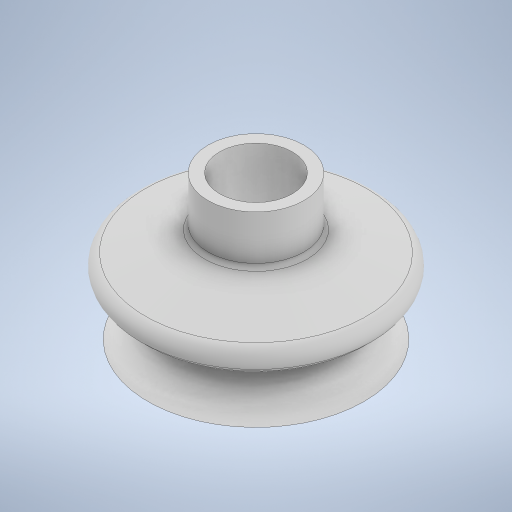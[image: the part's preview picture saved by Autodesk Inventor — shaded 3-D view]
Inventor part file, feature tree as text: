
AUTODESK INVENTOR PART (.ipt)
format: ipt  version: 2024 (Build 280153000, 153)  size: 373,248 bytes
history: native  units: mm
features: other x3, extrude x3, fillet x3, chamfer x2, revolve x1, hole x1, sketch x1
ambient origin geometry x8: Origin, YZ Plane, XZ Plane, XY Plane, X Axis, Y Axis, Z Axis, Center Point
bodies: Body1 (feature_tree)
feature tree (14):
  other  "Sólido1"
  extrude  "Extrusión1"  Depth=10.0mm TaperAngle=0.0deg
  extrude  "Extrusión2"  Depth=10.0mm
  extrude  "Extrusión3"  Depth=10.0mm TaperAngle=0.0deg
  chamfer  "Chaflán1"  Distance=20.0mm
  chamfer  "Chaflán2"  Distance=10.0mm
  fillet  "Empalme1"  Radius=15.0mm
  revolve  "Revolución1"  Angle=45.0deg
  fillet  "Empalme2"  Radius=2.5mm
  hole  "Agujero1"  [1 undecoded]
  fillet  "Empalme3"  [1 undecoded]
  other  "Edición directa1"
  sketch  "Boceto5"  dims[d0=45.0mm d1=10.0mm d2=0.0mm d3=50.0mm d4=10.0mm d5=0.0mm d6=20.0mm d7=10.0mm d8=0.0mm d9=15.0mm d10=5.0mm d11=45.0deg d12=2.5mm d13=7.75mm d14=45.0deg d15=2.5mm d16=5.0mm d17=90.0deg d18=2.0mm d19=15.1638mm d20=10.0mm d21=4.0mm d22=2.0mm d23=90.0deg d24=8.0mm d25=20.594885mm d26=1.0mm d27=2.66666mm d28=10.0mm d29=10.0mm]
  other  "Escala1"
note: 2 required parameter values undecoded (feature->parameter linkage not recoverable at this tier; creation-order binding heuristic only, values carry confidence <= 0.55)
